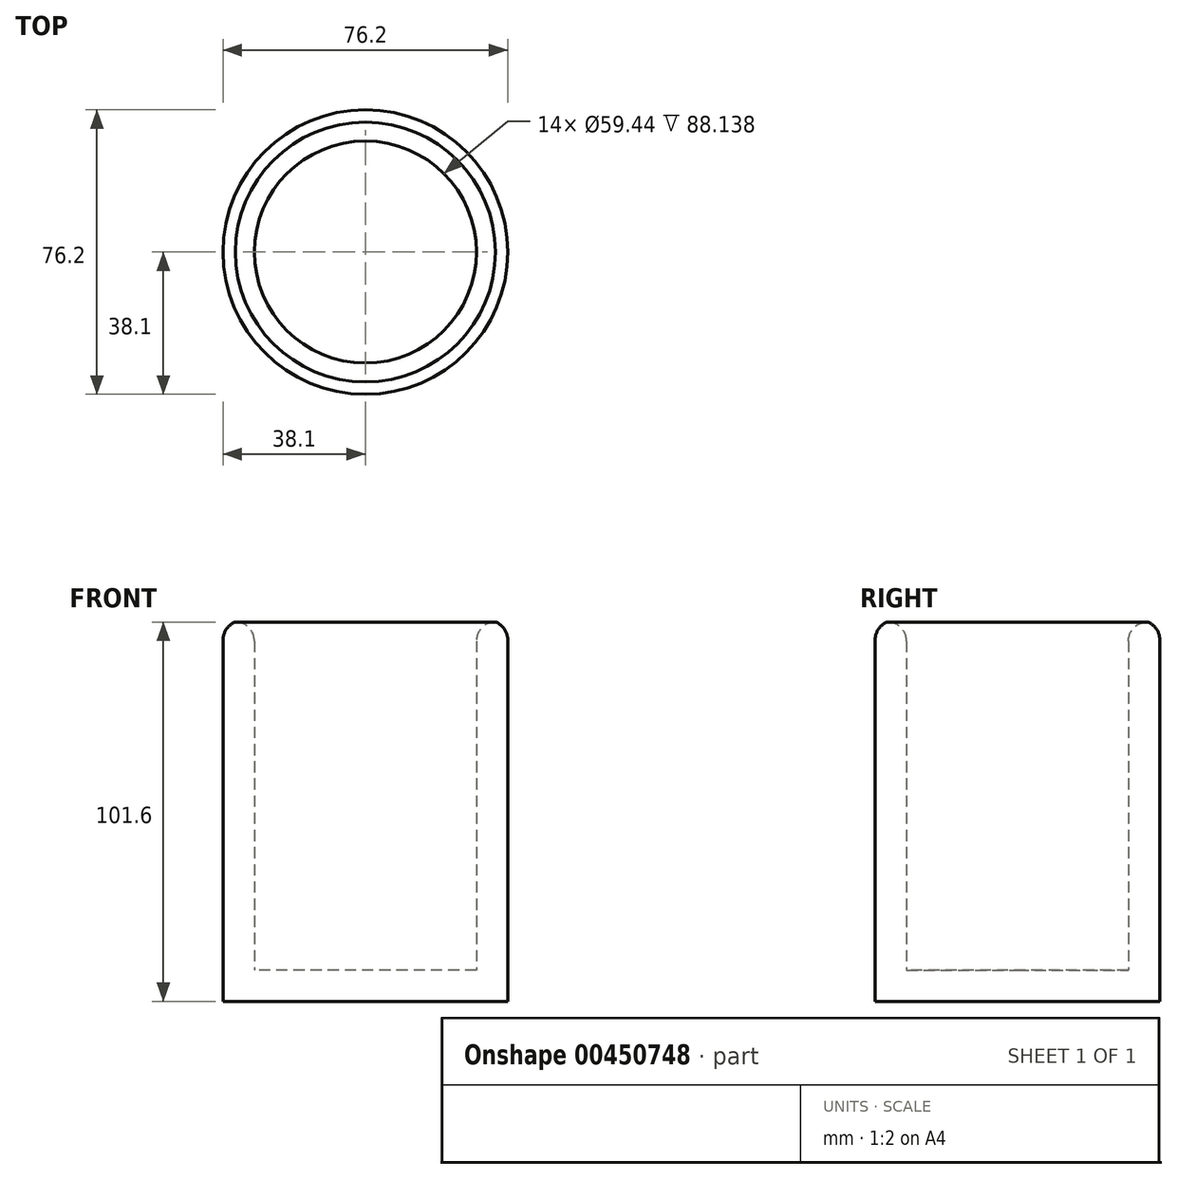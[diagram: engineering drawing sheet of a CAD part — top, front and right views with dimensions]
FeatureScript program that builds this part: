
annotation { "Feature Type Name" : "Feature", "Feature Type Description" : "" }
export const myFeature = defineFeature(function(context is Context, id is Id, definition is map)
    precondition{}
    {
        {
            var Q0;
            Q0=qCreatedBy(makeId("Top.planeOp"),FACE);
            var sketch = newSketch(context, id + "F0", { "sketchPlane" : qUnion([Q0])});
            skCircle(sketch, "E0", {"center": v(0, 0) * mm, "radius": 38.1 * mm});
            skSolve(sketch);
        }
        {
            var Q0;
            Q0=makeQuery(id+"F0.imprint","IMPRINT",FACE,{"disambiguationData":[TD([[makeQuery(id+"F0.imprint","IMPRINT",EDGE,{"derivedFrom":sQuery(id+"F0.wireOp",EDGE,"E0")}),1.0]])]});
            extrude(context, id + "F1", {"entities" : qUnion([Q0]), "depth" : 101.6 * mm});
        }
        {
            var Q0;
            Q0=makeQuery(id+"F1.opExtrude","CAP_FACE",FACE,{"disambiguationData":[OSD([sQuery(id+"F0.wireOp",EDGE,"E0")])],"isStart":false});
            shell(context, id + "F2", {"entities" : qUnion([Q0]), "thickness" : 8.38 * mm});
        }
        {
            var Q0;
            {var subQ0=sQuery(id+"F0.wireOp",EDGE,"E0");Q0=makeQuery(id+"F2.opShell","OFFSET_EDGE",EDGE,{"disambiguationData":[OSD([subQ0]),TDD([makeQuery(id+"F1.opExtrude","CAP_EDGE",EDGE,{"disambiguationData":[OSD([subQ0])],"isStart":false})])]});}
            fillet(context, id + "F3", {"entities" : qUnion([Q0]), "radius" : 5.08 * mm, "tangentPropagation" : true, "allowEdgeOverflow" : false});
        }
        {
            var Q0;
            Q0=makeQuery(id+"F1.opExtrude","CAP_EDGE",EDGE,{"disambiguationData":[OSD([sQuery(id+"F0.wireOp",EDGE,"E0")])],"isStart":false});
            fillet(context, id + "F4", {"entities" : qUnion([Q0]), "radius" : 5.08 * mm, "tangentPropagation" : true, "allowEdgeOverflow" : false});
        }
    });
